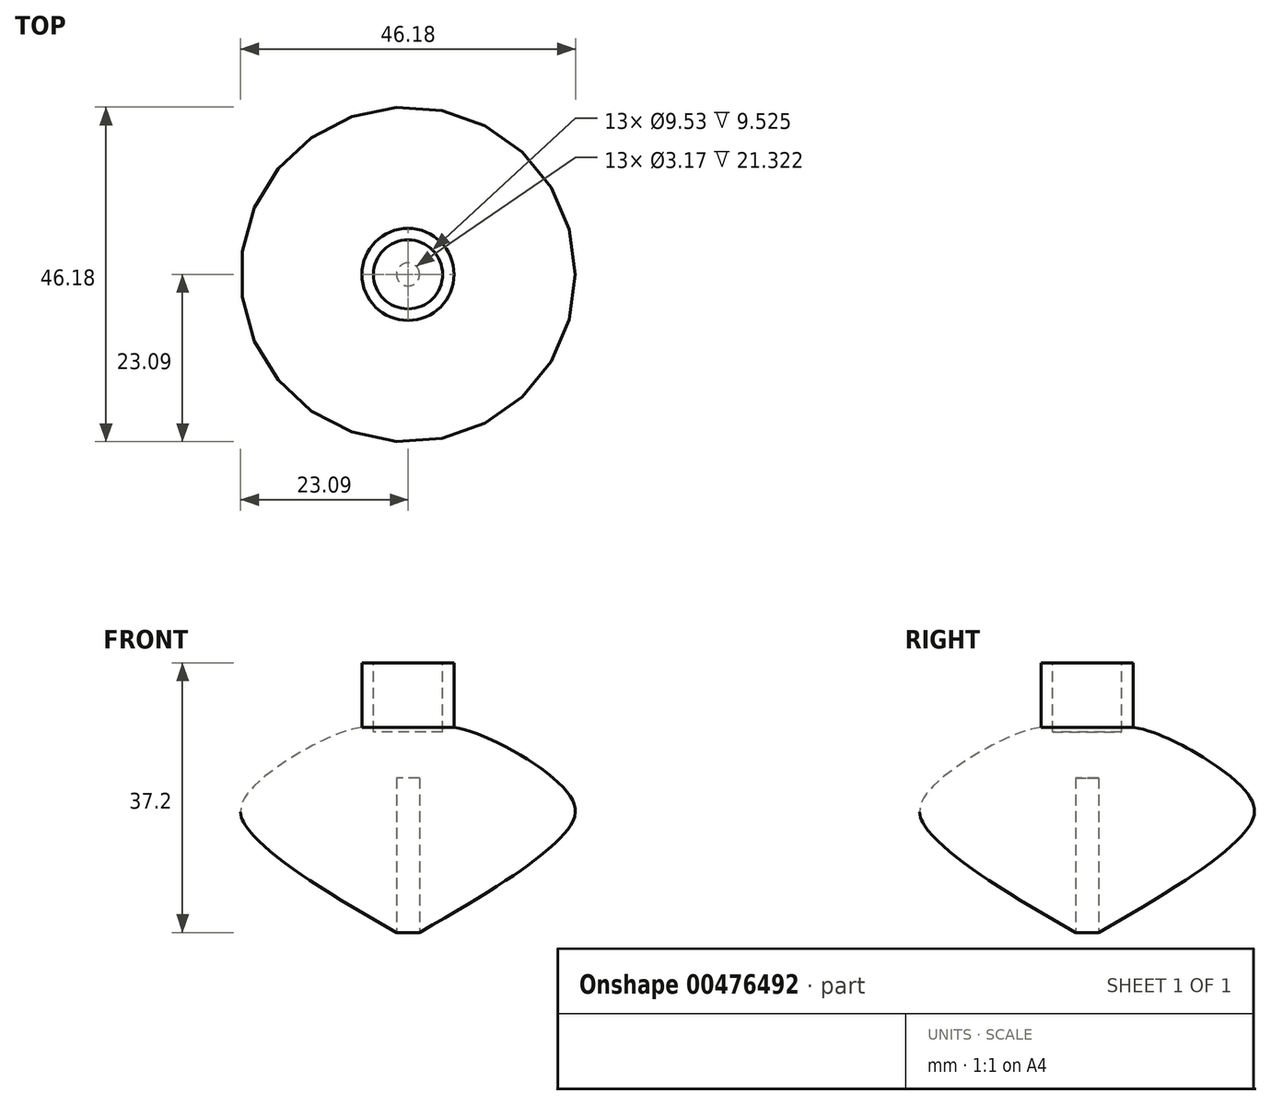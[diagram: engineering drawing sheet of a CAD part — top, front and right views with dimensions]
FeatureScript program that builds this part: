
annotation { "Feature Type Name" : "Feature", "Feature Type Description" : "" }
export const myFeature = defineFeature(function(context is Context, id is Id, definition is map)
    precondition{}
    {
        {
            var Q0;
            Q0=qCreatedBy(makeId("Front.planeOp"),FACE);
            var sketch = newSketch(context, id + "F0", { "sketchPlane" : qUnion([Q0])});
            skFitSpline(sketch, "E0", {"points": [v(0, 0) * mm, v(21.22, 14.16) * mm, v(22.56, 19.42) * mm, v(6.35, 29.21) * mm], "startDerivative": vector(81.94, 46.46) * mm, "endDerivative": vector(-34.66, 4.34) * mm});
            skLineSegment(sketch, "E1", {"start": v(6.35, 29.21) * mm, "end": v(6.35, 38.1) * mm});
            skLineSegment(sketch, "E2", {"start": v(6.35, 38.1) * mm, "end": v(0, 38.1) * mm});
            skLineSegment(sketch, "E3", {"start": v(0, 38.1) * mm, "end": v(0, 0) * mm});
            skLineSegment(sketch, "E4", {"start": v(23.08, 17.5) * mm, "end": v(23.08, 9.82) * mm});
            skSolve(sketch);
        }
        {
            var Q0;
            Q0 = qSketchRegion(id + "F0", true);
            var Q1;
            Q1=sQuery(id+"F0.wireOp",EDGE,"E3");
            revolve(context, id + "F1", {"entities" : qUnion([Q0]), "axis" : qUnion([Q1]), "revolveType" : RevolveType.FULL});
        }
        {
            var Q0;
            Q0=makeQuery(id+"F1.opRevolve","SWEPT_FACE",FACE,{"disambiguationData":[OSD([sQuery(id+"F0.wireOp",EDGE,"E2")])]});
            var sketch = newSketch(context, id + "F2", { "sketchPlane" : qUnion([Q0])});
            skCircle(sketch, "E5", {"center": v(0, 0) * mm, "radius": 4.76 * mm});
            skSolve(sketch);
        }
        {
            var Q0;
            Q0 = qSketchRegion(id + "F2", true);
            extrude(context, id + "F3", {"entities" : qUnion([Q0]), "operationType" : NewBodyOperationType.REMOVE, "oppositeDirection" : true, "depth" : 9.52 * mm});
        }
        {
            var Q0;
            Q0=qCreatedBy(makeId("Top.planeOp"),FACE);
            var sketch = newSketch(context, id + "F4", { "sketchPlane" : qUnion([Q0])});
            skCircle(sketch, "E6", {"center": v(0, 0) * mm, "radius": 1.59 * mm});
            skSolve(sketch);
        }
        {
            var Q0;
            Q0 = qSketchRegion(id + "F4", true);
            extrude(context, id + "F5", {"entities" : qUnion([Q0]), "operationType" : NewBodyOperationType.REMOVE, "depth" : 22.22 * mm});
        }
    });
